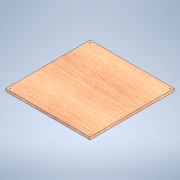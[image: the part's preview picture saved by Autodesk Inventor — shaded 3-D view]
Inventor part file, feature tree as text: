
AUTODESK INVENTOR PART (.ipt)
format: ipt  version: 2020 (Build 240168000, 168)  size: 131,072 bytes
history: native  units: mm
features: sketch x3, other x1, extrude x1, hole x1, projected_geometry x1
ambient origin geometry x8: Origin, YZ Plane, XZ Plane, XY Plane, X Axis, Y Axis, Z Axis, Center Point
bodies: Solid1 (feature_tree)
feature tree (7):
  other  "<userpath>\Documents\Development\paragon-printer\Paragon Printer Parameters.xlsx"
  sketch  "Sketch1"  dims[d0=400.0mm d1=400.0mm]
  extrude  "Extrusion1"  Depth=400.0mm
  hole  "Hole1"  [1 undecoded]
  sketch  "Sketch2"  dims[d2=12.7mm d3=0.0mm]
  sketch  "Sketch3"  dims[d4=10.0mm d5=3.4mm d6=6.0mm d7=6.3mm d8=2.0mm d9=90.0deg d10=8.0mm d11=20.594885mm]
  projected_geometry  "Projected Loop1"
note: 1 required parameter value undecoded (feature->parameter linkage not recoverable at this tier; creation-order binding heuristic only, values carry confidence <= 0.55)
